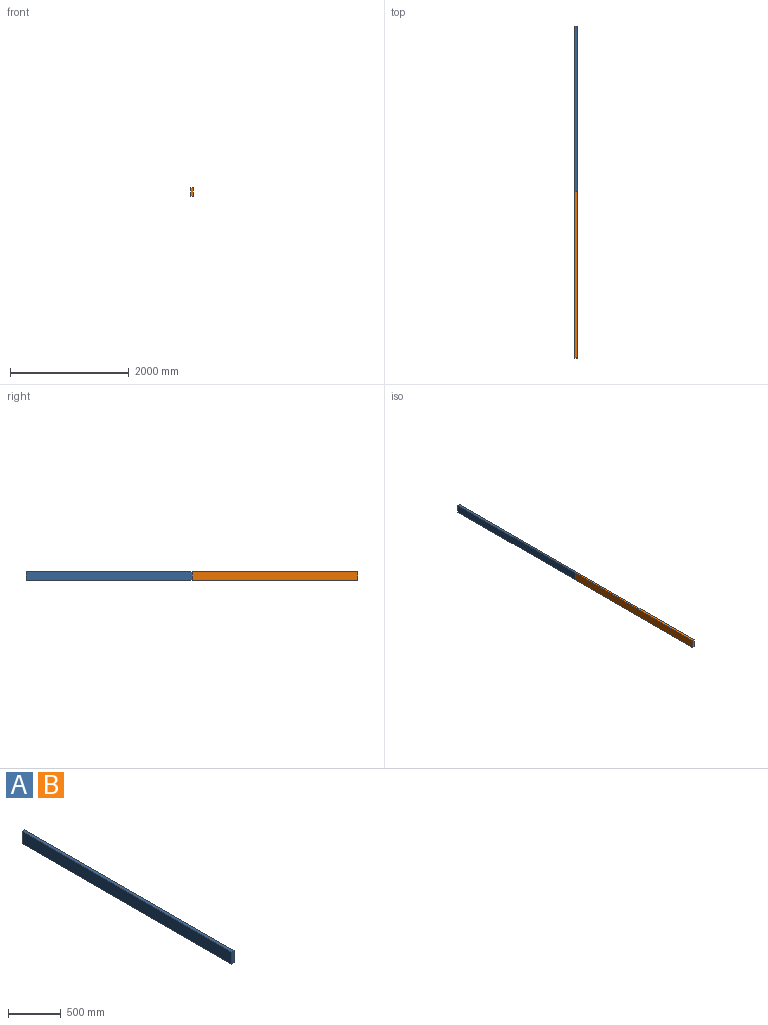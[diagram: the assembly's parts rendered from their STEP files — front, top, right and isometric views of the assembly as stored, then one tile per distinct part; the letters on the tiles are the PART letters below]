
ASSEMBLY  parts=2 mates=1
PART A: 6 faces, bbox 38.1x2794x139.7 mm
  f0: plane 2794x38.1mm, normal (0,0,1), area 106451.4mm2, adj f1,f3,f4,f5
  f1: plane 2794x139.7mm, normal (-1,0,0), area 390321.8mm2, adj f0,f2,f4,f5
  f2: plane 2794x38.1mm, normal (0,0,-1), area 106451.4mm2, adj f1,f3,f4,f5
  f3: plane 2794x139.7mm, normal (1,0,0), area 390321.8mm2, adj f0,f2,f4,f5
  f4: plane 139.7x38.1mm, normal (0,1,0), area 5322.6mm2, adj f0,f1,f2,f3
  f5: plane 139.7x38.1mm, normal (0,-1,0), area 5322.6mm2, adj f0,f1,f2,f3
PART B: same geometry as A
PLACE A t=(-161.85,-5444.82,1666.78)mm
PLACE B t=(-161.85,-8238.82,1666.78)mm
MATE fastened B.f4 <-> A.f5  axis (0,1,0) through (309.81,-5444.82,1318.08)mm
